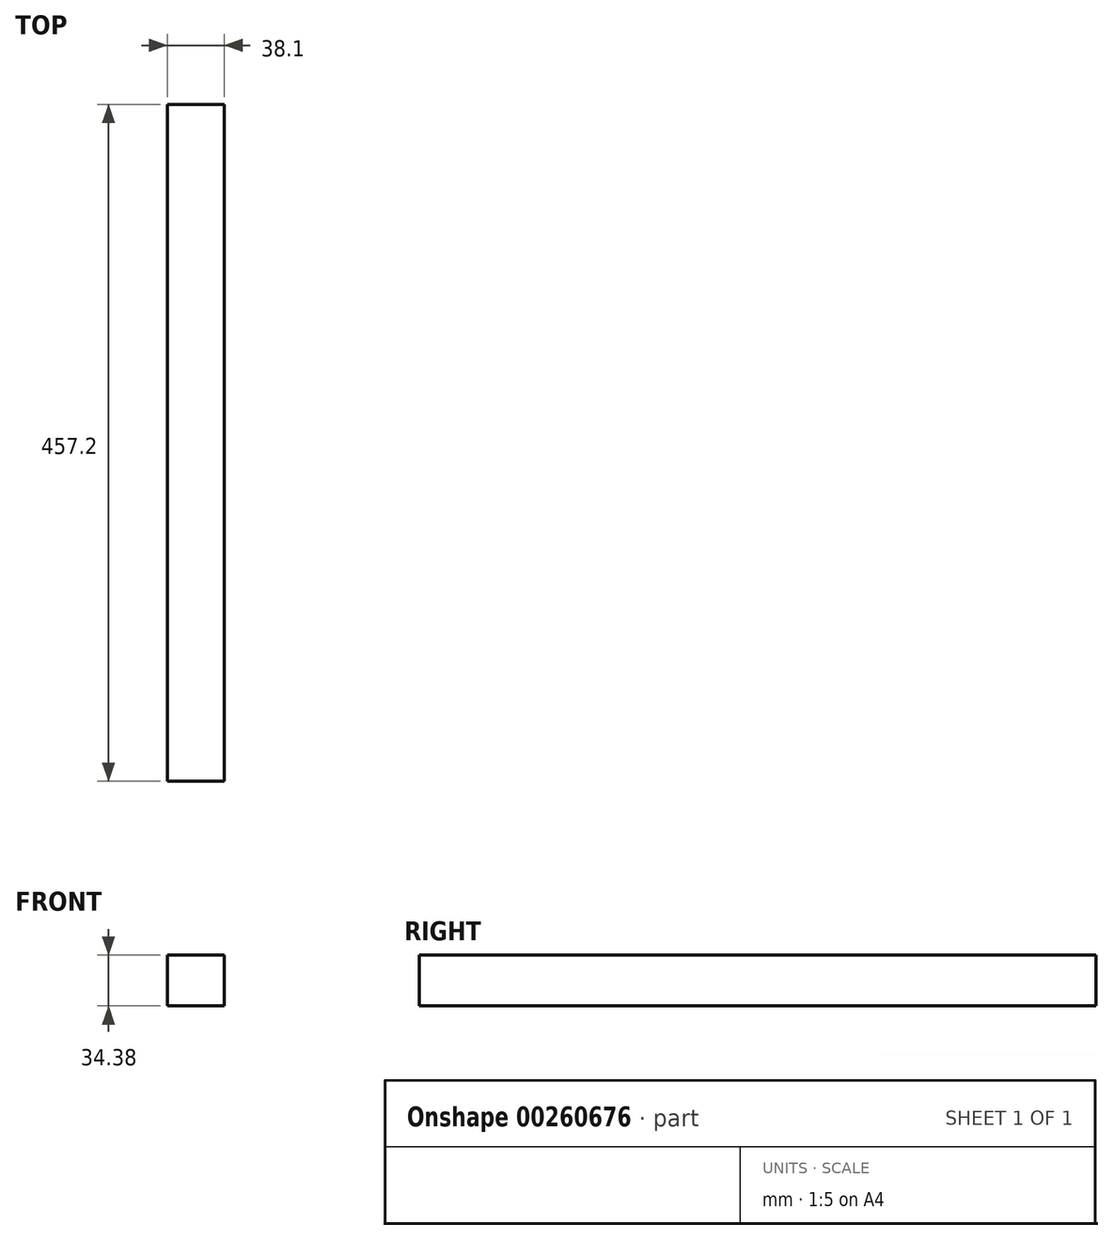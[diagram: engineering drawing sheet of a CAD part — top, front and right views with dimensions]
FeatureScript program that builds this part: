
annotation { "Feature Type Name" : "Feature", "Feature Type Description" : "" }
export const myFeature = defineFeature(function(context is Context, id is Id, definition is map)
    precondition{}
    {
        {
            var Q0;
            Q0=qCreatedBy(makeId("Front.planeOp"),FACE);
            var sketch = newSketch(context, id + "F0", { "sketchPlane" : qUnion([Q0])});
            skLineSegment(sketch, "E0.bottom", {"start": v(-11.47, 30.97) * mm, "end": v(26.63, 30.97) * mm});
            skLineSegment(sketch, "E0.top", {"start": v(-11.47, -3.41) * mm, "end": v(26.63, -3.41) * mm});
            skLineSegment(sketch, "E0.left", {"start": v(-11.47, 30.97) * mm, "end": v(-11.47, -3.41) * mm});
            skLineSegment(sketch, "E0.right", {"start": v(26.63, 30.97) * mm, "end": v(26.63, -3.41) * mm});
            skSolve(sketch);
        }
        {
            var Q0;
            Q0=makeQuery(id+"F0.imprint","IMPRINT",FACE,{"disambiguationData":[TD([[makeQuery(id+"F0.imprint","IMPRINT",EDGE,{"derivedFrom":sQuery(id+"F0.wireOp",EDGE,"E0.bottom")}),-1.0]])]});
            extrude(context, id + "F1", {"entities" : qUnion([Q0]), "depth" : 457.2 * mm});
        }
    });
